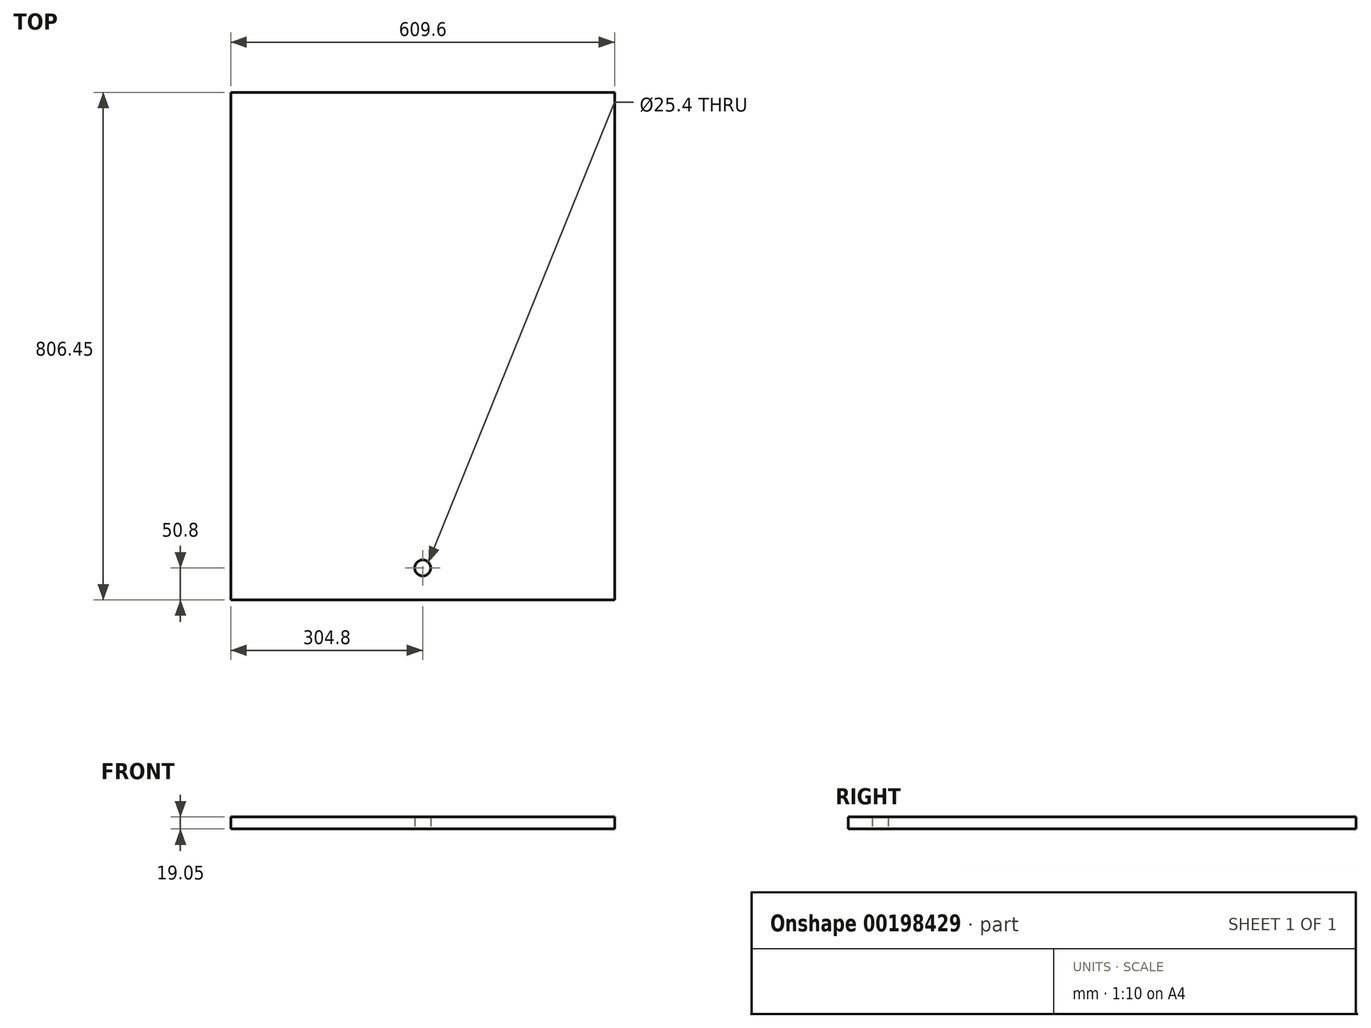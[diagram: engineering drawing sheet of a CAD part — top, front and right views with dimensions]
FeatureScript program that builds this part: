
annotation { "Feature Type Name" : "Feature", "Feature Type Description" : "" }
export const myFeature = defineFeature(function(context is Context, id is Id, definition is map)
    precondition{}
    {
        {
            var Q0;
            Q0=qCreatedBy(makeId("Top.planeOp"),FACE);
            var sketch = newSketch(context, id + "F0", { "sketchPlane" : qUnion([Q0])});
            skLineSegment(sketch, "E0.bottom", {"start": v(0, 0) * mm, "end": v(609.6, 0) * mm});
            skLineSegment(sketch, "E0.top", {"start": v(0, 806.45) * mm, "end": v(609.6, 806.45) * mm});
            skLineSegment(sketch, "E0.left", {"start": v(0, 0) * mm, "end": v(0, 806.45) * mm});
            skLineSegment(sketch, "E0.right", {"start": v(609.6, 0) * mm, "end": v(609.6, 806.45) * mm});
            skCircle(sketch, "E1", {"center": v(304.8, 50.8) * mm, "radius": 12.7 * mm});
            skSolve(sketch);
        }
        {
            var Q0;
            Q0 = qSketchRegion(id + "F0", true);
            extrude(context, id + "F1", {"entities" : qUnion([Q0]), "depth" : 19.05 * mm});
        }
    });
